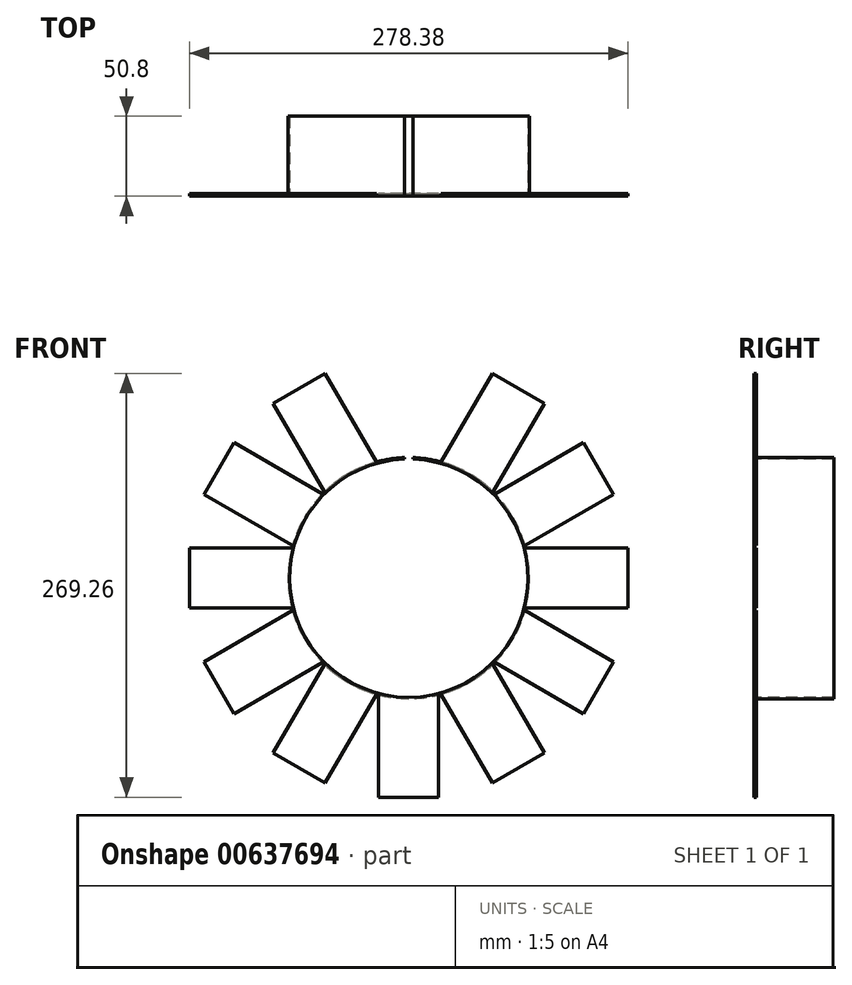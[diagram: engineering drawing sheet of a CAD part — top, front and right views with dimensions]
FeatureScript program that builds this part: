
annotation { "Feature Type Name" : "Feature", "Feature Type Description" : "" }
export const myFeature = defineFeature(function(context is Context, id is Id, definition is map)
    precondition{}
    {
        {
            var Q0;
            Q0=qCreatedBy(makeId("Front.planeOp"),FACE);
            var sketch = newSketch(context, id + "F0", { "sketchPlane" : qUnion([Q0])});
            skArc(sketch, "E0", {"start": v(-2.76, 75.64) * mm, "mid": v(0, -75.7) * mm, "end": v(2.76, 75.64) * mm});
            skArc(sketch, "E1", {"start": v(-2.8, 76.53) * mm, "mid": v(0, -76.58) * mm, "end": v(2.8, 76.53) * mm});
            skLineSegment(sketch, "E2", {"start": v(-2.8, 76.58) * mm, "end": v(-2.76, 75.64) * mm});
            skLineSegment(sketch, "E3.MirrorCS", {"start": v(2.8, 76.58) * mm, "end": v(2.76, 75.64) * mm});
            skPoint(sketch, "E4.start.orphan", {"position": v(0, 76.58) * mm});
            skLineSegment(sketch, "E5", {"start": v(-75.7, 0) * mm, "end": v(-139.2, 0) * mm});
            skLineSegment(sketch, "E6", {"start": v(-139.2, 0) * mm, "end": v(-139.2, -19.05) * mm});
            skLineSegment(sketch, "E7", {"start": v(-139.2, 0) * mm, "end": v(-139.2, 19.05) * mm});
            skLineSegment(sketch, "E8", {"start": v(-139.2, 19.05) * mm, "end": v(-74.17, 19.05) * mm});
            skLineSegment(sketch, "E9", {"start": v(-139.2, -19.05) * mm, "end": v(-74.17, -19.05) * mm});
            skLineSegment(sketch, "E10.1.0", {"start": v(-130.07, -53.1) * mm, "end": v(-73.76, -20.59) * mm});
            skLineSegment(sketch, "E10.1.1", {"start": v(-120.54, -69.6) * mm, "end": v(-130.07, -53.1) * mm});
            skLineSegment(sketch, "E10.1.2", {"start": v(-120.54, -69.6) * mm, "end": v(-111.02, -86.1) * mm});
            skLineSegment(sketch, "E10.1.3", {"start": v(-111.02, -86.1) * mm, "end": v(-54.71, -53.58) * mm});
            skLineSegment(sketch, "E10.2.0", {"start": v(-86.1, -111.02) * mm, "end": v(-53.58, -54.71) * mm});
            skLineSegment(sketch, "E10.2.1", {"start": v(-69.6, -120.54) * mm, "end": v(-86.1, -111.02) * mm});
            skLineSegment(sketch, "E10.2.2", {"start": v(-69.6, -120.54) * mm, "end": v(-53.1, -130.07) * mm});
            skLineSegment(sketch, "E10.2.3", {"start": v(-53.1, -130.07) * mm, "end": v(-20.59, -73.76) * mm});
            skLineSegment(sketch, "E10.3.0", {"start": v(-19.05, -139.2) * mm, "end": v(-19.05, -74.17) * mm});
            skLineSegment(sketch, "E10.3.1", {"start": v(0, -139.2) * mm, "end": v(-19.05, -139.2) * mm});
            skLineSegment(sketch, "E10.3.2", {"start": v(0, -139.2) * mm, "end": v(19.05, -139.2) * mm});
            skLineSegment(sketch, "E10.3.3", {"start": v(19.05, -139.2) * mm, "end": v(19.05, -74.17) * mm});
            skLineSegment(sketch, "E10.4.0", {"start": v(53.1, -130.07) * mm, "end": v(20.59, -73.76) * mm});
            skLineSegment(sketch, "E10.4.1", {"start": v(69.6, -120.54) * mm, "end": v(53.1, -130.07) * mm});
            skLineSegment(sketch, "E10.4.2", {"start": v(69.6, -120.54) * mm, "end": v(86.1, -111.02) * mm});
            skLineSegment(sketch, "E10.4.3", {"start": v(86.1, -111.02) * mm, "end": v(53.58, -54.71) * mm});
            skLineSegment(sketch, "E10.5.0", {"start": v(111.02, -86.1) * mm, "end": v(54.71, -53.58) * mm});
            skLineSegment(sketch, "E10.5.1", {"start": v(120.54, -69.6) * mm, "end": v(111.02, -86.1) * mm});
            skLineSegment(sketch, "E10.5.2", {"start": v(120.54, -69.6) * mm, "end": v(130.07, -53.1) * mm});
            skLineSegment(sketch, "E10.5.3", {"start": v(130.07, -53.1) * mm, "end": v(73.76, -20.59) * mm});
            skLineSegment(sketch, "E10.6.0", {"start": v(139.2, -19.05) * mm, "end": v(74.17, -19.05) * mm});
            skLineSegment(sketch, "E10.6.1", {"start": v(139.2, 0) * mm, "end": v(139.2, -19.05) * mm});
            skLineSegment(sketch, "E10.6.2", {"start": v(139.2, 0) * mm, "end": v(139.2, 19.05) * mm});
            skLineSegment(sketch, "E10.6.3", {"start": v(139.2, 19.05) * mm, "end": v(74.17, 19.05) * mm});
            skLineSegment(sketch, "E10.7.0", {"start": v(130.07, 53.1) * mm, "end": v(73.76, 20.59) * mm});
            skLineSegment(sketch, "E10.7.1", {"start": v(120.54, 69.6) * mm, "end": v(130.07, 53.1) * mm});
            skLineSegment(sketch, "E10.7.2", {"start": v(120.54, 69.6) * mm, "end": v(111.02, 86.1) * mm});
            skLineSegment(sketch, "E10.7.3", {"start": v(111.02, 86.1) * mm, "end": v(54.71, 53.58) * mm});
            skLineSegment(sketch, "E10.8.0", {"start": v(86.1, 111.02) * mm, "end": v(53.58, 54.71) * mm});
            skLineSegment(sketch, "E10.8.1", {"start": v(69.6, 120.54) * mm, "end": v(86.1, 111.02) * mm});
            skLineSegment(sketch, "E10.8.2", {"start": v(69.6, 120.54) * mm, "end": v(53.1, 130.07) * mm});
            skLineSegment(sketch, "E10.8.3", {"start": v(53.1, 130.07) * mm, "end": v(20.59, 73.76) * mm});
            skLineSegment(sketch, "E10.10.0", {"start": v(-53.1, 130.07) * mm, "end": v(-20.59, 73.76) * mm});
            skLineSegment(sketch, "E10.10.1", {"start": v(-69.6, 120.54) * mm, "end": v(-53.1, 130.07) * mm});
            skLineSegment(sketch, "E10.10.2", {"start": v(-69.6, 120.54) * mm, "end": v(-86.1, 111.02) * mm});
            skLineSegment(sketch, "E10.10.3", {"start": v(-86.1, 111.02) * mm, "end": v(-53.58, 54.71) * mm});
            skLineSegment(sketch, "E10.11.0", {"start": v(-111.02, 86.1) * mm, "end": v(-54.71, 53.58) * mm});
            skLineSegment(sketch, "E10.11.1", {"start": v(-120.54, 69.6) * mm, "end": v(-111.02, 86.1) * mm});
            skLineSegment(sketch, "E10.11.2", {"start": v(-120.54, 69.6) * mm, "end": v(-130.07, 53.1) * mm});
            skLineSegment(sketch, "E10.11.3", {"start": v(-130.07, 53.1) * mm, "end": v(-73.76, 20.59) * mm});
            skSolve(sketch);
        }
        {
            var Q0;
            {var subQ3=sQuery(id+"F0.wireOp",EDGE,"E2");var subQ4=sQuery(id+"F0.wireOp",EDGE,"E0");var subQ5=makeQuery(id+"F0.imprint","INTERSECT",VERTEX,{"derivedFrom":[subQ4,subQ3]});Q0=makeQuery(id+"F0.imprint","IMPRINT",FACE,{"disambiguationData":[TD([[makeQuery(id+"F0.imprint","IMPRINT",EDGE,{"disambiguationData":[TD([[subQ5,-1.0]])],"derivedFrom":subQ4}),-1.0]])]});}
            var Q1;
            {var subQ8=sQuery(id+"F0.wireOp",EDGE,"E3.MirrorCS");var subQ9=sQuery(id+"F0.wireOp",EDGE,"E0");var subQ10=makeQuery(id+"F0.imprint","INTERSECT",VERTEX,{"derivedFrom":[subQ9,subQ8]});Q1=makeQuery(id+"F0.imprint","IMPRINT",FACE,{"disambiguationData":[TD([[makeQuery(id+"F0.imprint","IMPRINT",EDGE,{"disambiguationData":[TD([[subQ10,1.0]])],"derivedFrom":subQ9}),-1.0]])]});}
            var Q2;
            Q2=sQuery(id+"F0.wireOp",EDGE,"E1");
            extrude(context, id + "F1", {"entities" : qUnion([Q0, Q1]), "surfaceEntities" : qUnion([Q2]), "oppositeDirection" : true, "depth" : 50.8 * mm, "offsetDistance" : 25.4 * mm});
        }
        {
            var Q0;
            Q0 = qSketchRegion(id + "F0", true);
            extrude(context, id + "F2", {"entities" : qUnion([Q0]), "operationType" : NewBodyOperationType.ADD, "oppositeDirection" : true, "depth" : 1.78 * mm, "offsetDistance" : 25.4 * mm});
        }
    });
